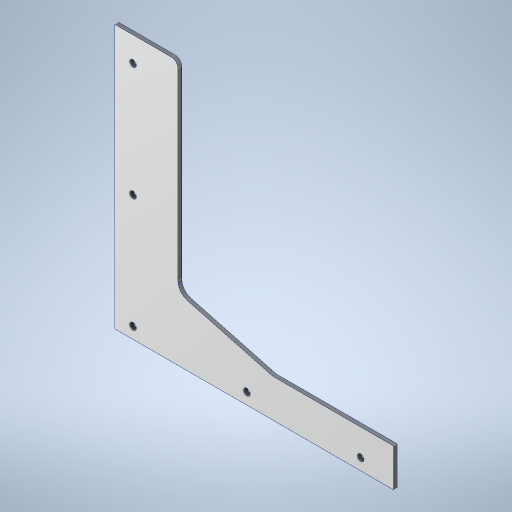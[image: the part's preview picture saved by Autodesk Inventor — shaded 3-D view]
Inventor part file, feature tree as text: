
AUTODESK INVENTOR PART (.ipt)
format: ipt  version: 2024 (Build 280153000, 153)  size: 316,416 bytes
history: native  units: mm
features: extrude x3, other x2, sketch x2, fillet x2, hole x1
ambient origin geometry x8: Origin, YZ Plane, XZ Plane, XY Plane, X Axis, Y Axis, Z Axis, Center Point
bodies: Body1 (feature_tree), Body2 (feature_tree)
feature tree (10):
  other  "Laminate"
  sketch  "Sketch1"  dims[d2=3.0mm d3=0.0mm d4=2.9mm d5=0.0mm]
  extrude  "Extrusion1"  Depth=2.9mm TaperAngle=0.0deg
  extrude  "Extrusion2"  Depth=220.5mm
  extrude  "Extrusion3"  Depth=208.5mm
  fillet  "Fillet1"  Radius=30.0mm
  fillet  "Fillet2"  [1 undecoded]
  hole  "Hole6"  [1 undecoded]
  other  "Core"
  sketch  "Sketch11"  dims[d6=2.9mm d7=0.0mm d101=220.5mm d102=208.5mm d103=30.0mm d105=165.0deg d106=50.0mm d107=75.0mm d108=10.0mm d109=5.0mm d110=50.0mm d112=45.0mm d113=10.0mm d115=10.0mm d117=9.0mm d118=14.5mm d119=50.0mm d121=45.0mm d122=10.0mm d124=10.0mm d126=5.3mm d127=10.0mm d128=4.0mm d129=2.0mm d130=90.0deg d131=8.0mm d132=20.594885mm]
note: 2 required parameter values undecoded (feature->parameter linkage not recoverable at this tier; creation-order binding heuristic only, values carry confidence <= 0.55)
